# Revit family: Kanalhalter Z
name_source: partatom
category: Allgemeines Modell
revit_build: Autodesk Revit 2017 (Build: 20190507_1515(x64)
units: mm (PartAtom-declared; Revit-internal decimal feet)

## family parameters
Arbeitsebenenbasiert = Ja
Beim Laden mit Abzugskörper schneiden = Nein
Bemaßung runder Anschluss = Durchmesser verwenden
Gemeinsam genutzt = Ja
Immer vertikal = Nein
Kann Basisbauteil für Bewehrung sein = Nein
Raumberechnungspunkt = Nein
Teiletyp = Normal

## types (1)
- Kanalhalter Z
    Anschluss = M8/M10
    Artikelnummer = 05900280
    Ausführung = leicht
    Bauart = Z
    Breite Material = 30 mm
    Dämmelementtyp = gesteckt
    EAN = 4250928415004
    Fabrikat = MEFA
    Firma = MEFA Befestigungs- und Montagesysteme GmbH
    Gewicht = 0.08 kg
    Gewicht pro Bauteil = 0.08 kg
    Höhe = 30 mm
    Kurztext1 = Kanalhalter Z
    Kurztext2 = Höhe 30 mm Gummi gesteckt
    Länge = 74 mm
    Mengeneinheit = St
    Schalldämmeinlage = Gummi EPDM
    Stärke Material = 3 mm  [stored 0.00984252 ft]
    Vorgabe-Ansicht = 1219 mm
    max. Temperaturbeständigkeit = 100 °C
    max. zul. Last hängend = 7.00 kN
    max. zul. Last stehend = 0.00 kN
    vpe = 50 St

note: [stored X ft] marks values corroborated as IEEE doubles in the binary element streams (Revit-internal decimal feet)
